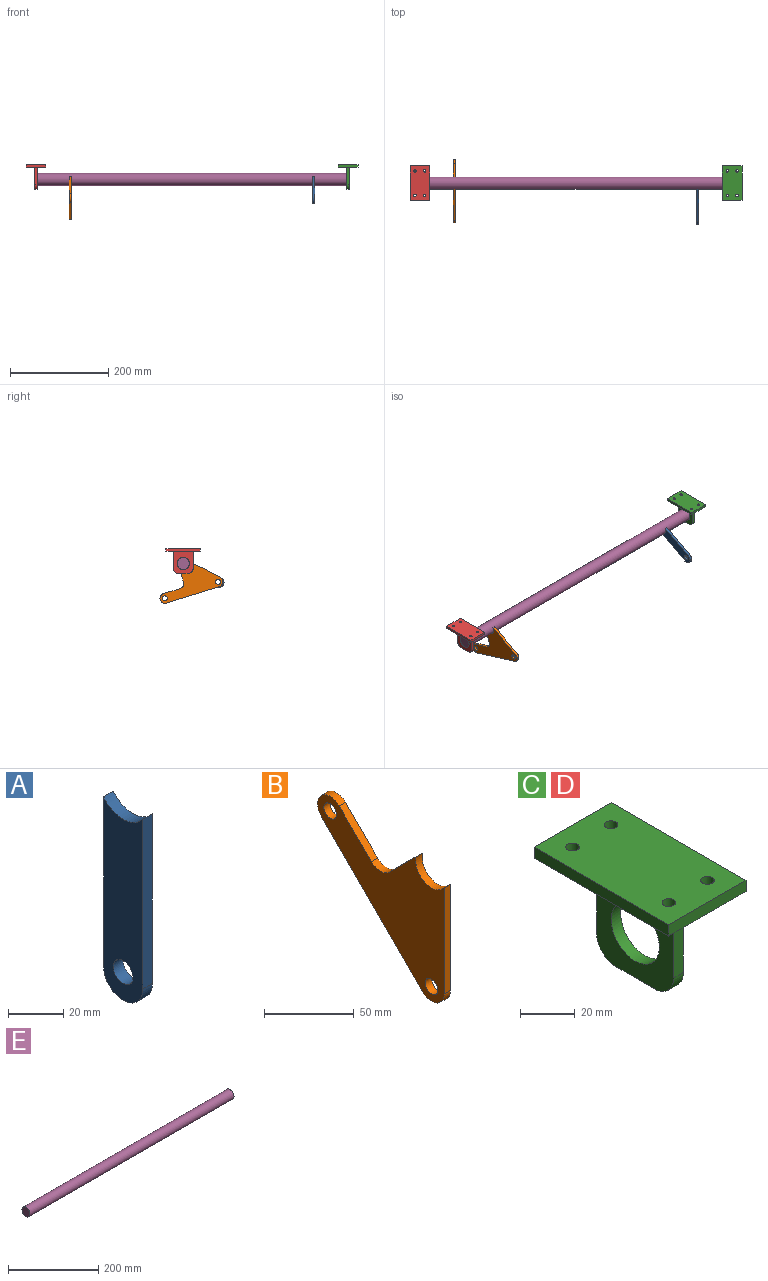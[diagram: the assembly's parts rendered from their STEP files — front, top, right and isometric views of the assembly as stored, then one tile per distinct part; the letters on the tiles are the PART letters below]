
ASSEMBLY  parts=5 mates=3
PART A: 7 faces, bbox 5x20x85 mm
  f0: cylinder r=12.5mm len=20mm, axis (-1,0,0), area 115.9mm2, adj f1,f3,f5,f6
  f1: plane 75x5mm, normal (0,-1,0), area 375mm2, adj f0,f2,f5,f6
  f2: cylinder r=10mm len=20mm, axis (-1,0,0), area 157.1mm2, adj f1,f3,f5,f6
  f3: plane 75x5mm, normal (0,1,0), area 375mm2, adj f0,f2,f5,f6
  f4: cylinder r=5mm len=10mm, axis (-1,0,0), area 157.1mm2, adj f5,f6
  f5: plane 85x20mm, normal (1,0,0), area 1508.6mm2, adj f0,f1,f2,f3,f4
  f6: plane 85x20mm, normal (-1,0,0), area 1508.6mm2, adj f0,f1,f2,f3,f4
PART B: 12 faces, bbox 5x100x100 mm
  f0: cylinder r=12.5mm len=22.5mm, axis (-1,0,0), area 169.4mm2, adj f1,f8,f10,f11
  f1: plane 72.5x5mm, normal (0,-1,0), area 362.5mm2, adj f0,f2,f10,f11
  f2: cylinder r=10mm len=17.07mm, axis (-1,0,0), area 117.8mm2, adj f1,f3,f10,f11
  f3: plane 80x80mm, normal (0,0.71,-0.71), area 565.7mm2, adj f2,f4,f10,f11
  f4: cylinder r=10mm len=17.07mm, axis (-1,0,0), area 157.1mm2, adj f3,f5,f10,f11
  f5: plane 25.5x25.5mm, normal (0,-0.71,0.71), area 180.3mm2, adj f4,f6,f10,f11
  f6: cylinder r=10mm len=14.14mm, axis (-1,0,0), area 78.5mm2, adj f5,f8,f10,f11
  f7: cylinder r=5mm len=10mm, axis (-1,0,0), area 157.1mm2, adj f10,f11
  f8: plane 21.07x21.07mm, normal (0,0.71,0.71), area 149mm2, adj f0,f6,f10,f11
  f9: cylinder r=5mm len=10mm, axis (-1,0,0), area 157.1mm2, adj f10,f11
  f10: plane 100x100mm, normal (1,0,0), area 4440.6mm2, adj f0,f1,f2,f3,f4,f5,f6,f7
  f11: plane 100x100mm, normal (-1,0,0), area 4440.6mm2, adj f0,f1,f2,f3,f4,f5,f6,f7
PART C: 18 faces, bbox 40x70x50 mm
  f0: plane 40x5mm, normal (0,-1,0), area 200mm2, adj f1,f7,f8,f9
  f1: plane 70x5mm, normal (-1,0,0), area 350mm2, adj f0,f2,f8,f9
  f2: plane 40x5mm, normal (0,1,0), area 200mm2, adj f1,f7,f8,f9
  f3: cylinder r=2.5mm len=5mm, axis (0,0,1), area 78.5mm2, adj f8,f9
  f4: cylinder r=2.5mm len=5mm, axis (0,0,1), area 78.5mm2, adj f8,f9
  f5: cylinder r=2.5mm len=5mm, axis (0,0,1), area 78.5mm2, adj f8,f9
  f6: cylinder r=2.5mm len=5mm, axis (0,0,1), area 78.5mm2, adj f8,f9
  f7: plane 70x5mm, normal (1,0,0), area 350mm2, adj f0,f2,f8,f9
  f8: plane 70x40mm, normal (0,0,-1), area 2521.5mm2, adj f0,f1,f2,f3,f4,f5,f6,f7
  f9: plane 70x40mm, normal (0,0,1), area 2721.5mm2, adj f0,f1,f2,f3,f4,f5,f6,f7
  f10: plane 20x5mm, normal (0,0,-1), area 100mm2, adj f11,f13,f16,f17
  f11: plane 45x40mm, normal (1,0,0), area 1266.2mm2, adj f8,f10,f12,f14,f15,f16,f17
  f12: plane 35x5mm, normal (0,1,0), area 175mm2, adj f8,f11,f13,f16
  f13: plane 45x40mm, normal (-1,0,0), area 1266.2mm2, adj f8,f10,f12,f14,f15,f16,f17
  f14: plane 35x5mm, normal (0,-1,0), area 175mm2, adj f8,f11,f13,f17
  f15: cylinder r=12.5mm len=25mm, axis (-1,0,0), area 392.7mm2, adj f11,f13
  f16: cylinder r=10mm len=10mm, axis (-1,0,0), area 78.5mm2, adj f10,f11,f12,f13
  f17: cylinder r=10mm len=10mm, axis (1,0,0), area 78.5mm2, adj f10,f11,f13,f14
PART D: same geometry as C
PART E: 3 faces, bbox 640x25x25 mm
  f0: cylinder r=12.5mm len=640mm, axis (-1,0,0), area 50265.5mm2, adj f1,f2
  f1: plane 25x25mm, normal (1,0,0), area 490.9mm2, adj f0
  f2: plane 25x25mm, normal (-1,0,0), area 490.9mm2, adj f0
PLACE A rot(axis=(-1,0,0),62.2deg) t=(655,-238.89,-489.45)mm
PLACE B rot(axis=(-1,0,0),62.2deg) t=(160,-80,-264.62)mm
PLACE C t=(1510.14,389.12,-126.15)mm
PLACE D t=(875.14,389.12,-126.15)mm
PLACE E rot(axis=(1,0,0),27.8deg) t=(90,231.11,141.49)mm
MATE revolute E.f0 <-> C.f15  axis (-1,0,0) through (730,-220.93,-156.15)mm
MATE fastened E.f0 <-> A.f0  axis (-1,0,0) through (730,-220.93,-156.15)mm
MATE fastened E.f0 <-> B.f0  axis (-1,0,0) through (730,-220.93,-156.15)mm
